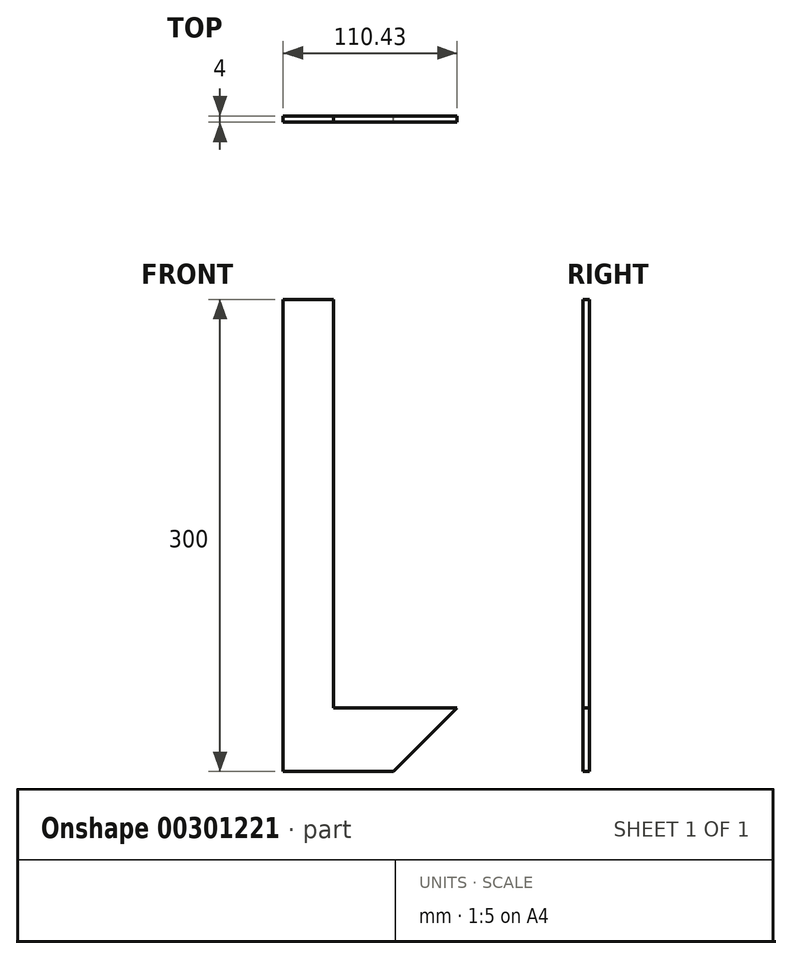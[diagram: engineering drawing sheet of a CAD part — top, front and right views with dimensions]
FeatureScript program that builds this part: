
annotation { "Feature Type Name" : "Feature", "Feature Type Description" : "" }
export const myFeature = defineFeature(function(context is Context, id is Id, definition is map)
    precondition{}
    {
        {
            var Q0;
            Q0=qCreatedBy(makeId("Front.planeOp"),FACE);
            var sketch = newSketch(context, id + "F0", { "sketchPlane" : qUnion([Q0])});
            skLineSegment(sketch, "E0", {"start": v(-4.42, 239.29) * mm, "end": v(27.58, 239.29) * mm});
            skLineSegment(sketch, "E1", {"start": v(-4.42, 239.29) * mm, "end": v(-4.42, -60.71) * mm});
            skLineSegment(sketch, "E2", {"start": v(-4.42, -60.71) * mm, "end": v(65.58, -60.71) * mm});
            skLineSegment(sketch, "E3", {"start": v(65.58, -60.71) * mm, "end": v(106, -20.28) * mm});
            skLineSegment(sketch, "E4", {"start": v(106, -20.28) * mm, "end": v(27.58, -20.28) * mm});
            skLineSegment(sketch, "E5", {"start": v(27.58, -20.28) * mm, "end": v(27.58, 239.29) * mm});
            skSolve(sketch);
        }
        {
            var Q0;
            Q0=makeQuery(id+"F0.imprint","IMPRINT",FACE,{"disambiguationData":[TD([[makeQuery(id+"F0.imprint","IMPRINT",EDGE,{"derivedFrom":sQuery(id+"F0.wireOp",EDGE,"E0")}),-1.0]])]});
            extrude(context, id + "F1", {"entities" : qUnion([Q0]), "depth" : 4 * mm});
        }
    });
